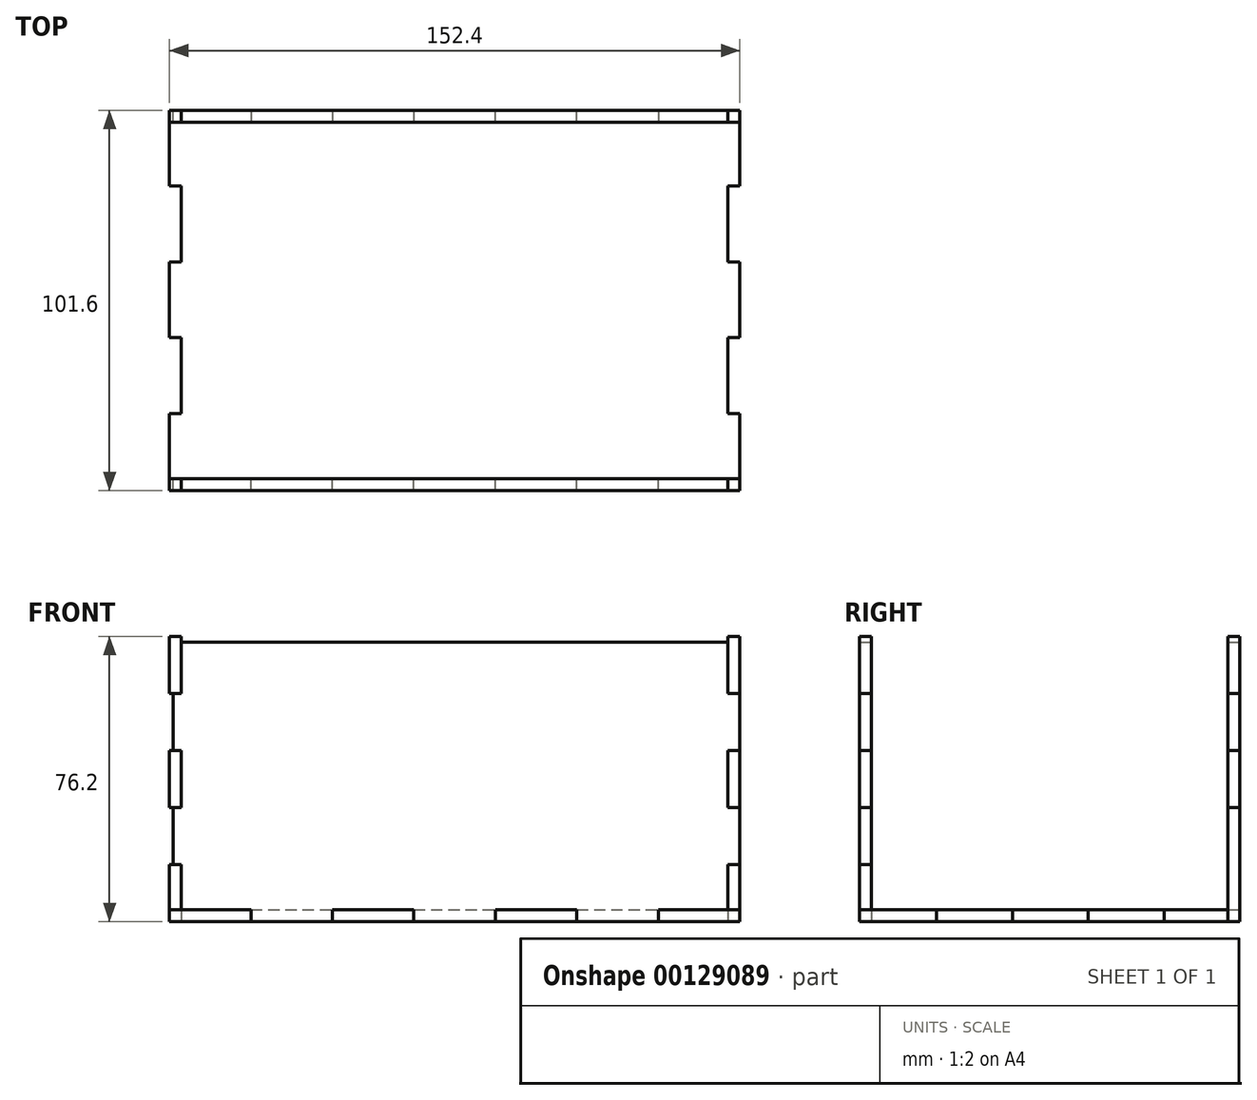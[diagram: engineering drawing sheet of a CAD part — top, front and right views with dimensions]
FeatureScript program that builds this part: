
annotation { "Feature Type Name" : "Feature", "Feature Type Description" : "" }
export const myFeature = defineFeature(function(context is Context, id is Id, definition is map)
    precondition{}
    {
        {
            var Q0;
            Q0=qCreatedBy(makeId("Top.planeOp"),FACE);
            var sketch = newSketch(context, id + "F0", { "sketchPlane" : qUnion([Q0])});
            skLineSegment(sketch, "E0.bottom", {"start": v(76.2, 50.8) * mm, "end": v(-76.2, 50.8) * mm});
            skLineSegment(sketch, "E0.top", {"start": v(76.2, -50.8) * mm, "end": v(-76.2, -50.8) * mm});
            skLineSegment(sketch, "E0.left", {"start": v(76.2, 50.8) * mm, "end": v(76.2, -50.8) * mm});
            skLineSegment(sketch, "E0.right", {"start": v(-76.2, 50.8) * mm, "end": v(-76.2, -50.8) * mm});
            skPoint(sketch, "E0.middle", {"position": v(0, 0) * mm});
            skLineSegment(sketch, "E1", {"start": v(-76.2, 50.8) * mm, "end": v(-73.03, 50.8) * mm});
            skLineSegment(sketch, "E2.0.1.0", {"start": v(-76.2, 30.55) * mm, "end": v(-73.03, 30.55) * mm});
            skLineSegment(sketch, "E2.0.2.0", {"start": v(-76.2, 10.3) * mm, "end": v(-73.03, 10.3) * mm});
            skLineSegment(sketch, "E2.0.3.0", {"start": v(-76.2, -9.95) * mm, "end": v(-73.03, -9.95) * mm});
            skLineSegment(sketch, "E2.0.4.0", {"start": v(-76.2, -30.2) * mm, "end": v(-73.03, -30.2) * mm});
            skLineSegment(sketch, "E2.0.5.0", {"start": v(-76.2, -50.45) * mm, "end": v(-73.03, -50.45) * mm});
            skLineSegment(sketch, "E2.direction1", {"start": v(-76.2, 50.8) * mm, "end": v(-47.87, 50.8) * mm});
            skLineSegment(sketch, "E2.direction2", {"start": v(-76.2, 50.8) * mm, "end": v(-76.2, 30.55) * mm, "construction": true});
            skLineSegment(sketch, "E3", {"start": v(-73.03, 50.8) * mm, "end": v(-73.03, -50.45) * mm});
            skLineSegment(sketch, "E4.MirrorCS", {"start": v(76.2, 50.8) * mm, "end": v(73.03, 50.8) * mm});
            skLineSegment(sketch, "E5.MirrorCS", {"start": v(76.2, -50.45) * mm, "end": v(73.03, -50.45) * mm});
            skLineSegment(sketch, "E6.MirrorCS", {"start": v(76.2, 30.55) * mm, "end": v(73.03, 30.55) * mm});
            skLineSegment(sketch, "E7.MirrorCS", {"start": v(76.2, -9.95) * mm, "end": v(73.03, -9.95) * mm});
            skLineSegment(sketch, "E8.MirrorCS", {"start": v(76.2, 10.3) * mm, "end": v(73.03, 10.3) * mm});
            skLineSegment(sketch, "E9.MirrorCS", {"start": v(76.2, -30.2) * mm, "end": v(73.03, -30.2) * mm});
            skLineSegment(sketch, "E10.MirrorCS", {"start": v(73.03, 50.8) * mm, "end": v(73.03, -50.45) * mm});
            skLineSegment(sketch, "E11.MirrorCS", {"start": v(76.2, 50.8) * mm, "end": v(76.2, 30.55) * mm, "construction": true});
            skLineSegment(sketch, "E12", {"start": v(-76.2, 50.8) * mm, "end": v(-76.2, 47.63) * mm});
            skLineSegment(sketch, "E13.1.0.0", {"start": v(-54.43, 50.8) * mm, "end": v(-54.43, 47.63) * mm});
            skLineSegment(sketch, "E13.2.0.0", {"start": v(-32.66, 50.8) * mm, "end": v(-32.66, 47.63) * mm});
            skLineSegment(sketch, "E13.3.0.0", {"start": v(-10.89, 50.8) * mm, "end": v(-10.89, 47.63) * mm});
            skLineSegment(sketch, "E13.4.0.0", {"start": v(10.89, 50.8) * mm, "end": v(10.89, 47.63) * mm});
            skLineSegment(sketch, "E13.5.0.0", {"start": v(32.66, 50.8) * mm, "end": v(32.66, 47.63) * mm});
            skLineSegment(sketch, "E13.6.0.0", {"start": v(54.43, 50.8) * mm, "end": v(54.43, 47.63) * mm});
            skLineSegment(sketch, "E13.7.0.0", {"start": v(76.2, 50.8) * mm, "end": v(76.2, 47.63) * mm});
            skLineSegment(sketch, "E13.direction1", {"start": v(-76.2, 47.62) * mm, "end": v(-54.43, 47.62) * mm, "construction": true});
            skLineSegment(sketch, "E14", {"start": v(-76.2, 47.62) * mm, "end": v(76.2, 47.63) * mm});
            skLineSegment(sketch, "E15.MirrorCS", {"start": v(76.2, -50.8) * mm, "end": v(76.2, -47.63) * mm});
            skLineSegment(sketch, "E16.MirrorCS", {"start": v(-76.2, -50.8) * mm, "end": v(-73.03, -50.8) * mm});
            skLineSegment(sketch, "E17.MirrorCS", {"start": v(-76.2, -50.8) * mm, "end": v(-76.2, -47.63) * mm});
            skLineSegment(sketch, "E18.MirrorCS", {"start": v(76.2, -50.8) * mm, "end": v(73.03, -50.8) * mm});
            skLineSegment(sketch, "E19.MirrorCS", {"start": v(-54.43, -50.8) * mm, "end": v(-54.43, -47.63) * mm});
            skLineSegment(sketch, "E20.MirrorCS", {"start": v(-32.66, -50.8) * mm, "end": v(-32.66, -47.63) * mm});
            skLineSegment(sketch, "E21.MirrorCS", {"start": v(54.43, -50.8) * mm, "end": v(54.43, -47.63) * mm});
            skLineSegment(sketch, "E22.MirrorCS", {"start": v(32.66, -50.8) * mm, "end": v(32.66, -47.63) * mm});
            skLineSegment(sketch, "E23.MirrorCS", {"start": v(-10.89, -50.8) * mm, "end": v(-10.89, -47.63) * mm});
            skLineSegment(sketch, "E24.MirrorCS", {"start": v(10.89, -50.8) * mm, "end": v(10.89, -47.63) * mm});
            skLineSegment(sketch, "E25.MirrorCS", {"start": v(-76.2, -47.62) * mm, "end": v(-54.43, -47.62) * mm, "construction": true});
            skLineSegment(sketch, "E26.MirrorCS", {"start": v(-76.2, -47.62) * mm, "end": v(76.2, -47.63) * mm});
            skLineSegment(sketch, "E27.MirrorCS", {"start": v(-76.2, -50.8) * mm, "end": v(-47.87, -50.8) * mm});
            skSolve(sketch);
        }
        {
            var Q0;
            {var subQ3=sQuery(id+"F0.wireOp",EDGE,"E2.0.1.0");Q0=makeQuery(id+"F0.imprint","IMPRINT",FACE,{"disambiguationData":[TD([[makeQuery(id+"F0.imprint","IMPRINT",EDGE,{"derivedFrom":subQ3}),1.0]])]});}
            var Q1;
            {var subQ3=sQuery(id+"F0.wireOp",EDGE,"E13.1.0.0");Q1=makeQuery(id+"F0.imprint","IMPRINT",FACE,{"disambiguationData":[TD([[makeQuery(id+"F0.imprint","IMPRINT",EDGE,{"derivedFrom":subQ3}),-1.0]])]});}
            var Q2;
            {var subQ0=sQuery(id+"F0.wireOp",EDGE,"E12");Q2=makeQuery(id+"F0.imprint","IMPRINT",FACE,{"disambiguationData":[TD([[makeQuery(id+"F0.imprint","IMPRINT",EDGE,{"derivedFrom":subQ0}),1.0]])]});}
            var Q3;
            {var subQ0=sQuery(id+"F0.wireOp",EDGE,"E13.2.0.0");Q3=makeQuery(id+"F0.imprint","IMPRINT",FACE,{"disambiguationData":[TD([[makeQuery(id+"F0.imprint","IMPRINT",EDGE,{"derivedFrom":subQ0}),1.0]])]});}
            var Q4;
            {var subQ15=sQuery(id+"F0.wireOp",EDGE,"E3");var subQ24=makeQuery(id+"F0.imprint","INTERSECT",VERTEX,{"derivedFrom":[sQuery(id+"F0.wireOp",EDGE,"E2.0.1.0"),subQ15]});Q4=makeQuery(id+"F0.imprint","IMPRINT",FACE,{"disambiguationData":[TD([[makeQuery(id+"F0.imprint","IMPRINT",EDGE,{"disambiguationData":[TD([[subQ24,1.0]])],"derivedFrom":subQ15}),1.0]])]});}
            var Q5;
            {var subQ0=sQuery(id+"F0.wireOp",EDGE,"E13.4.0.0");Q5=makeQuery(id+"F0.imprint","IMPRINT",FACE,{"disambiguationData":[TD([[makeQuery(id+"F0.imprint","IMPRINT",EDGE,{"derivedFrom":subQ0}),1.0]])]});}
            var Q6;
            {var subQ3=sQuery(id+"F0.wireOp",EDGE,"E13.6.0.0");Q6=makeQuery(id+"F0.imprint","IMPRINT",FACE,{"disambiguationData":[TD([[makeQuery(id+"F0.imprint","IMPRINT",EDGE,{"derivedFrom":subQ3}),1.0]])]});}
            var Q7;
            {var subQ0=sQuery(id+"F0.wireOp",EDGE,"E4.MirrorCS");Q7=makeQuery(id+"F0.imprint","IMPRINT",FACE,{"disambiguationData":[TD([[makeQuery(id+"F0.imprint","IMPRINT",EDGE,{"derivedFrom":subQ0}),1.0]])]});}
            var Q8;
            {var subQ0=sQuery(id+"F0.wireOp",EDGE,"E6.MirrorCS");Q8=makeQuery(id+"F0.imprint","IMPRINT",FACE,{"disambiguationData":[TD([[makeQuery(id+"F0.imprint","IMPRINT",EDGE,{"derivedFrom":subQ0}),-1.0]])]});}
            var Q9;
            {var subQ0=sQuery(id+"F0.wireOp",EDGE,"E7.MirrorCS");Q9=makeQuery(id+"F0.imprint","IMPRINT",FACE,{"disambiguationData":[TD([[makeQuery(id+"F0.imprint","IMPRINT",EDGE,{"derivedFrom":subQ0}),-1.0]])]});}
            var Q10;
            {var subQ0=sQuery(id+"F0.wireOp",EDGE,"E9.MirrorCS");Q10=makeQuery(id+"F0.imprint","IMPRINT",FACE,{"disambiguationData":[TD([[makeQuery(id+"F0.imprint","IMPRINT",EDGE,{"derivedFrom":subQ0}),1.0]])]});}
            var Q11;
            {var subQ0=sQuery(id+"F0.wireOp",EDGE,"E5.MirrorCS");Q11=makeQuery(id+"F0.imprint","IMPRINT",FACE,{"disambiguationData":[TD([[makeQuery(id+"F0.imprint","IMPRINT",EDGE,{"derivedFrom":subQ0}),-1.0]])]});}
            var Q12;
            {var subQ2=sQuery(id+"F0.wireOp",EDGE,"E5.MirrorCS");Q12=makeQuery(id+"F0.imprint","IMPRINT",FACE,{"disambiguationData":[TD([[makeQuery(id+"F0.imprint","IMPRINT",EDGE,{"derivedFrom":subQ2}),1.0]])]});}
            var Q13;
            {var subQ0=sQuery(id+"F0.wireOp",EDGE,"E22.MirrorCS");Q13=makeQuery(id+"F0.imprint","IMPRINT",FACE,{"disambiguationData":[TD([[makeQuery(id+"F0.imprint","IMPRINT",EDGE,{"derivedFrom":subQ0}),1.0]])]});}
            var Q14;
            {var subQ0=sQuery(id+"F0.wireOp",EDGE,"E20.MirrorCS");Q14=makeQuery(id+"F0.imprint","IMPRINT",FACE,{"disambiguationData":[TD([[makeQuery(id+"F0.imprint","IMPRINT",EDGE,{"derivedFrom":subQ0}),-1.0]])]});}
            var Q15;
            {var subQ5=sQuery(id+"F0.wireOp",EDGE,"E2.0.5.0");Q15=makeQuery(id+"F0.imprint","IMPRINT",FACE,{"disambiguationData":[TD([[makeQuery(id+"F0.imprint","IMPRINT",EDGE,{"derivedFrom":subQ5}),-1.0]])]});}
            var Q16;
            {var subQ0=sQuery(id+"F0.wireOp",EDGE,"E2.0.5.0");Q16=makeQuery(id+"F0.imprint","IMPRINT",FACE,{"disambiguationData":[TD([[makeQuery(id+"F0.imprint","IMPRINT",EDGE,{"derivedFrom":subQ0}),1.0]])]});}
            var Q17;
            {var subQ3=sQuery(id+"F0.wireOp",EDGE,"E2.0.4.0");Q17=makeQuery(id+"F0.imprint","IMPRINT",FACE,{"disambiguationData":[TD([[makeQuery(id+"F0.imprint","IMPRINT",EDGE,{"derivedFrom":subQ3}),-1.0]])]});}
            var Q18;
            {var subQ0=sQuery(id+"F0.wireOp",EDGE,"E2.0.2.0");Q18=makeQuery(id+"F0.imprint","IMPRINT",FACE,{"disambiguationData":[TD([[makeQuery(id+"F0.imprint","IMPRINT",EDGE,{"derivedFrom":subQ0}),-1.0]])]});}
            extrude(context, id + "F1", {"entities" : qUnion([Q0, Q1, Q2, Q3, Q4, Q5, Q6, Q7, Q8, Q9, Q10, Q11, Q12, Q13, Q14, Q15, Q16, Q17, Q18]), "depth" : 3.17 * mm});
        }
        {
            var Q0;
            Q0=makeQuery(id+"F1.opExtrude","SWEPT_FACE",FACE,{"disambiguationData":[OSD([sQuery(id+"F0.wireOp",EDGE,"E0.left"),sQuery(id+"F0.wireOp",EDGE,"E15.MirrorCS")])]});
            var sketch = newSketch(context, id + "F2", { "sketchPlane" : qUnion([Q0])});
            skLineSegment(sketch, "E28.bottom", {"start": v(-50.8, 0) * mm, "end": v(50.8, 0) * mm});
            skLineSegment(sketch, "E28.top", {"start": v(-50.8, 76.2) * mm, "end": v(50.8, 76.2) * mm});
            skLineSegment(sketch, "E28.left", {"start": v(-50.8, 0) * mm, "end": v(-50.8, 76.2) * mm});
            skLineSegment(sketch, "E28.right", {"start": v(50.8, 0) * mm, "end": v(50.8, 76.2) * mm});
            skLineSegment(sketch, "E29", {"start": v(-50.8, 76.2) * mm, "end": v(-47.63, 76.2) * mm});
            skLineSegment(sketch, "E30.0.1.0", {"start": v(-50.8, 60.96) * mm, "end": v(-47.63, 60.96) * mm});
            skLineSegment(sketch, "E30.0.2.0", {"start": v(-50.8, 45.72) * mm, "end": v(-47.63, 45.72) * mm});
            skLineSegment(sketch, "E30.0.3.0", {"start": v(-50.8, 30.48) * mm, "end": v(-47.63, 30.48) * mm});
            skLineSegment(sketch, "E30.0.4.0", {"start": v(-50.8, 15.24) * mm, "end": v(-47.63, 15.24) * mm});
            skLineSegment(sketch, "E30.0.5.0", {"start": v(-50.8, 0) * mm, "end": v(-47.63, 0) * mm});
            skLineSegment(sketch, "E30.direction1", {"start": v(-50.8, 76.2) * mm, "end": v(-25.4, 76.2) * mm, "construction": true});
            skLineSegment(sketch, "E30.direction2", {"start": v(-50.8, 76.2) * mm, "end": v(-50.8, 60.96) * mm, "construction": true});
            skLineSegment(sketch, "E31", {"start": v(-47.63, 0) * mm, "end": v(-47.63, 76.2) * mm});
            skLineSegment(sketch, "E32.MirrorCS", {"start": v(50.8, 76.2) * mm, "end": v(47.63, 76.2) * mm});
            skLineSegment(sketch, "E33.MirrorCS", {"start": v(50.8, 0) * mm, "end": v(47.63, 0) * mm});
            skLineSegment(sketch, "E34.MirrorCS", {"start": v(50.8, 60.96) * mm, "end": v(47.63, 60.96) * mm});
            skLineSegment(sketch, "E35.MirrorCS", {"start": v(50.8, 45.72) * mm, "end": v(47.63, 45.72) * mm});
            skLineSegment(sketch, "E36.MirrorCS", {"start": v(50.8, 30.48) * mm, "end": v(47.63, 30.48) * mm});
            skLineSegment(sketch, "E37.MirrorCS", {"start": v(50.8, 15.24) * mm, "end": v(47.63, 15.24) * mm});
            skLineSegment(sketch, "E38.MirrorCS", {"start": v(47.63, 0) * mm, "end": v(47.63, 76.2) * mm});
            skLineSegment(sketch, "E39.MirrorCS", {"start": v(50.8, 76.2) * mm, "end": v(50.8, 60.96) * mm, "construction": true});
            skSolve(sketch);
        }
        {
            var Q0;
            {var subQ4=sQuery(id+"F2.wireOp",EDGE,"E28.top");Q0=makeQuery(id+"F2.imprint","IMPRINT",FACE,{"disambiguationData":[TD([[makeQuery(id+"F2.imprint","IMPRINT",EDGE,{"derivedFrom":subQ4}),-1.0]])]});}
            var Q1;
            {var subQ0=sQuery(id+"F2.wireOp",EDGE,"E29");Q1=makeQuery(id+"F2.imprint","IMPRINT",FACE,{"disambiguationData":[TD([[makeQuery(id+"F2.imprint","IMPRINT",EDGE,{"derivedFrom":subQ0}),-1.0]])]});}
            var Q2;
            {var subQ0=sQuery(id+"F2.wireOp",EDGE,"E30.0.2.0");Q2=makeQuery(id+"F2.imprint","IMPRINT",FACE,{"disambiguationData":[TD([[makeQuery(id+"F2.imprint","IMPRINT",EDGE,{"derivedFrom":subQ0}),-1.0]])]});}
            var Q3;
            {var subQ3=sQuery(id+"F2.wireOp",EDGE,"E30.0.4.0");Q3=makeQuery(id+"F2.imprint","IMPRINT",FACE,{"disambiguationData":[TD([[makeQuery(id+"F2.imprint","IMPRINT",EDGE,{"derivedFrom":subQ3}),-1.0]])]});}
            var Q4;
            {var subQ0=sQuery(id+"F2.wireOp",EDGE,"E32.MirrorCS");Q4=makeQuery(id+"F2.imprint","IMPRINT",FACE,{"disambiguationData":[TD([[makeQuery(id+"F2.imprint","IMPRINT",EDGE,{"derivedFrom":subQ0}),1.0]])]});}
            var Q5;
            {var subQ0=sQuery(id+"F2.wireOp",EDGE,"E35.MirrorCS");Q5=makeQuery(id+"F2.imprint","IMPRINT",FACE,{"disambiguationData":[TD([[makeQuery(id+"F2.imprint","IMPRINT",EDGE,{"derivedFrom":subQ0}),1.0]])]});}
            var Q6;
            {var subQ0=sQuery(id+"F2.wireOp",EDGE,"E33.MirrorCS");Q6=makeQuery(id+"F2.imprint","IMPRINT",FACE,{"disambiguationData":[TD([[makeQuery(id+"F2.imprint","IMPRINT",EDGE,{"derivedFrom":subQ0}),-1.0]])]});}
            extrude(context, id + "F3", {"entities" : qUnion([Q0, Q1, Q2, Q3, Q4, Q5, Q6]), "oppositeDirection" : true, "depth" : 3.17 * mm});
        }
        {
            var Q0;
            Q0=makeQuery(id+"F3.opExtrude","SWEPT_BODY",BODY,{"disambiguationData":[OSD([sQuery(id+"F0.wireOp",EDGE,"E9.MirrorCS"),sQuery(id+"F0.wireOp",EDGE,"E0.left"),sQuery(id+"F0.wireOp",EDGE,"E15.MirrorCS"),sQuery(id+"F2.wireOp",EDGE,"E28.bottom"),sQuery(id+"F2.wireOp",EDGE,"E28.top"),sQuery(id+"F2.wireOp",EDGE,"E28.left"),sQuery(id+"F2.wireOp",EDGE,"E29"),sQuery(id+"F2.wireOp",EDGE,"E30.0.1.0"),sQuery(id+"F2.wireOp",EDGE,"E30.0.2.0"),sQuery(id+"F2.wireOp",EDGE,"E30.0.3.0"),sQuery(id+"F2.wireOp",EDGE,"E30.0.4.0"),sQuery(id+"F2.wireOp",EDGE,"E31"),sQuery(id+"F2.wireOp",EDGE,"E32.MirrorCS"),sQuery(id+"F2.wireOp",EDGE,"E33.MirrorCS"),sQuery(id+"F2.wireOp",EDGE,"E34.MirrorCS"),sQuery(id+"F2.wireOp",EDGE,"E35.MirrorCS"),sQuery(id+"F2.wireOp",EDGE,"E36.MirrorCS"),sQuery(id+"F2.wireOp",EDGE,"E37.MirrorCS"),sQuery(id+"F2.wireOp",EDGE,"E28.right"),sQuery(id+"F2.wireOp",EDGE,"E38.MirrorCS")])]});
            var Q1;
            Q1=qCreatedBy(makeId("Right.planeOp"),FACE);
            mirror(context, id + "F4", {"entities" : qUnion([Q0]), "mirrorPlane" : qUnion([Q1])});
        }
        {
            var Q0;
            Q0=makeQuery(id+"F1.opExtrude","SWEPT_BODY",BODY,{"disambiguationData":[OSD([sQuery(id+"F0.wireOp",EDGE,"E0.bottom"),sQuery(id+"F0.wireOp",EDGE,"E0.right"),sQuery(id+"F0.wireOp",EDGE,"E2.0.1.0"),sQuery(id+"F0.wireOp",EDGE,"E2.0.2.0"),sQuery(id+"F0.wireOp",EDGE,"E2.0.3.0"),sQuery(id+"F0.wireOp",EDGE,"E2.0.4.0"),sQuery(id+"F0.wireOp",EDGE,"E2.direction1"),sQuery(id+"F0.wireOp",EDGE,"E3"),sQuery(id+"F0.wireOp",EDGE,"E4.MirrorCS"),sQuery(id+"F0.wireOp",EDGE,"E6.MirrorCS"),sQuery(id+"F0.wireOp",EDGE,"E7.MirrorCS"),sQuery(id+"F0.wireOp",EDGE,"E8.MirrorCS"),sQuery(id+"F0.wireOp",EDGE,"E9.MirrorCS"),sQuery(id+"F0.wireOp",EDGE,"E10.MirrorCS"),sQuery(id+"F0.wireOp",EDGE,"E0.left"),sQuery(id+"F0.wireOp",EDGE,"E12"),sQuery(id+"F0.wireOp",EDGE,"E13.1.0.0"),sQuery(id+"F0.wireOp",EDGE,"E13.2.0.0"),sQuery(id+"F0.wireOp",EDGE,"E13.3.0.0"),sQuery(id+"F0.wireOp",EDGE,"E13.4.0.0"),sQuery(id+"F0.wireOp",EDGE,"E13.5.0.0"),sQuery(id+"F0.wireOp",EDGE,"E13.6.0.0"),sQuery(id+"F0.wireOp",EDGE,"E13.7.0.0"),sQuery(id+"F0.wireOp",EDGE,"E14"),sQuery(id+"F0.wireOp",EDGE,"E15.MirrorCS"),sQuery(id+"F0.wireOp",EDGE,"E17.MirrorCS"),sQuery(id+"F0.wireOp",EDGE,"E19.MirrorCS"),sQuery(id+"F0.wireOp",EDGE,"E20.MirrorCS"),sQuery(id+"F0.wireOp",EDGE,"E21.MirrorCS"),sQuery(id+"F0.wireOp",EDGE,"E22.MirrorCS"),sQuery(id+"F0.wireOp",EDGE,"E23.MirrorCS"),sQuery(id+"F0.wireOp",EDGE,"E24.MirrorCS"),sQuery(id+"F0.wireOp",EDGE,"E26.MirrorCS"),sQuery(id+"F0.wireOp",EDGE,"E0.top")])]});
            var Q1;
            Q1=makeQuery(id+"F3.opExtrude","SWEPT_BODY",BODY,{"disambiguationData":[OSD([sQuery(id+"F0.wireOp",EDGE,"E9.MirrorCS"),sQuery(id+"F0.wireOp",EDGE,"E0.left"),sQuery(id+"F0.wireOp",EDGE,"E15.MirrorCS"),sQuery(id+"F2.wireOp",EDGE,"E28.bottom"),sQuery(id+"F2.wireOp",EDGE,"E28.top"),sQuery(id+"F2.wireOp",EDGE,"E28.left"),sQuery(id+"F2.wireOp",EDGE,"E29"),sQuery(id+"F2.wireOp",EDGE,"E30.0.1.0"),sQuery(id+"F2.wireOp",EDGE,"E30.0.2.0"),sQuery(id+"F2.wireOp",EDGE,"E30.0.3.0"),sQuery(id+"F2.wireOp",EDGE,"E30.0.4.0"),sQuery(id+"F2.wireOp",EDGE,"E31"),sQuery(id+"F2.wireOp",EDGE,"E32.MirrorCS"),sQuery(id+"F2.wireOp",EDGE,"E33.MirrorCS"),sQuery(id+"F2.wireOp",EDGE,"E34.MirrorCS"),sQuery(id+"F2.wireOp",EDGE,"E35.MirrorCS"),sQuery(id+"F2.wireOp",EDGE,"E36.MirrorCS"),sQuery(id+"F2.wireOp",EDGE,"E37.MirrorCS"),sQuery(id+"F2.wireOp",EDGE,"E28.right"),sQuery(id+"F2.wireOp",EDGE,"E38.MirrorCS")])]});
            var Q2;
            Q2=makeQuery(id+"F4.opPattern","COPY",BODY,{"derivedFrom":makeQuery(id+"F3.opExtrude","SWEPT_BODY",BODY,{"disambiguationData":[OSD([sQuery(id+"F0.wireOp",EDGE,"E9.MirrorCS"),sQuery(id+"F0.wireOp",EDGE,"E0.left"),sQuery(id+"F0.wireOp",EDGE,"E15.MirrorCS"),sQuery(id+"F2.wireOp",EDGE,"E28.bottom"),sQuery(id+"F2.wireOp",EDGE,"E28.top"),sQuery(id+"F2.wireOp",EDGE,"E28.left"),sQuery(id+"F2.wireOp",EDGE,"E29"),sQuery(id+"F2.wireOp",EDGE,"E30.0.1.0"),sQuery(id+"F2.wireOp",EDGE,"E30.0.2.0"),sQuery(id+"F2.wireOp",EDGE,"E30.0.3.0"),sQuery(id+"F2.wireOp",EDGE,"E30.0.4.0"),sQuery(id+"F2.wireOp",EDGE,"E31"),sQuery(id+"F2.wireOp",EDGE,"E32.MirrorCS"),sQuery(id+"F2.wireOp",EDGE,"E33.MirrorCS"),sQuery(id+"F2.wireOp",EDGE,"E34.MirrorCS"),sQuery(id+"F2.wireOp",EDGE,"E35.MirrorCS"),sQuery(id+"F2.wireOp",EDGE,"E36.MirrorCS"),sQuery(id+"F2.wireOp",EDGE,"E37.MirrorCS"),sQuery(id+"F2.wireOp",EDGE,"E28.right"),sQuery(id+"F2.wireOp",EDGE,"E38.MirrorCS")])]}),"instanceName":"1"});
            booleanBodies(context, id + "F5", {"operationType" : BooleanOperationType.SUBTRACTION, "tools" : qUnion([Q0]), "targets" : qUnion([Q1, Q2]), "keepTools" : true});
        }
        {
            var Q0;
            Q0=makeQuery(id+"F1.opExtrude","SWEPT_FACE",FACE,{"disambiguationData":[OSD([sQuery(id+"F0.wireOp",EDGE,"E0.bottom"),sQuery(id+"F0.wireOp",EDGE,"E4.MirrorCS")])]});
            var sketch = newSketch(context, id + "F6", { "sketchPlane" : qUnion([Q0])});
            skLineSegment(sketch, "E40.bottom", {"start": v(-76.2, 74.64) * mm, "end": v(75.17, 74.64) * mm});
            skLineSegment(sketch, "E40.top", {"start": v(-76.2, 0) * mm, "end": v(75.17, 0) * mm});
            skLineSegment(sketch, "E40.left", {"start": v(-76.2, 74.64) * mm, "end": v(-76.2, 0) * mm});
            skLineSegment(sketch, "E40.right", {"start": v(75.17, 74.64) * mm, "end": v(75.17, 0) * mm});
            skSolve(sketch);
        }
        {
            var Q0;
            {var subQ4=sQuery(id+"F6.wireOp",EDGE,"E40.bottom");Q0=makeQuery(id+"F6.imprint","IMPRINT",FACE,{"disambiguationData":[TD([[makeQuery(id+"F6.imprint","IMPRINT",EDGE,{"derivedFrom":subQ4}),-1.0]])]});}
            extrude(context, id + "F7", {"entities" : qUnion([Q0]), "oppositeDirection" : true, "depth" : 3.17 * mm});
        }
        {
            var Q0;
            Q0=makeQuery(id+"F7.opExtrude","SWEPT_BODY",BODY,{"disambiguationData":[OSD([sQuery(id+"F0.wireOp",EDGE,"E0.bottom"),sQuery(id+"F0.wireOp",EDGE,"E4.MirrorCS"),sQuery(id+"F0.wireOp",EDGE,"E13.6.0.0"),sQuery(id+"F6.wireOp",EDGE,"E40.bottom"),sQuery(id+"F6.wireOp",EDGE,"E40.top"),sQuery(id+"F6.wireOp",EDGE,"E40.left"),sQuery(id+"F6.wireOp",EDGE,"E40.right")])]});
            var Q1;
            Q1=qCreatedBy(makeId("Front.planeOp"),FACE);
            mirror(context, id + "F8", {"entities" : qUnion([Q0]), "mirrorPlane" : qUnion([Q1])});
        }
        {
            var Q0;
            Q0=makeQuery(id+"F3.opExtrude","SWEPT_BODY",BODY,{"disambiguationData":[OSD([sQuery(id+"F0.wireOp",EDGE,"E9.MirrorCS"),sQuery(id+"F0.wireOp",EDGE,"E0.left"),sQuery(id+"F0.wireOp",EDGE,"E15.MirrorCS"),sQuery(id+"F2.wireOp",EDGE,"E28.bottom"),sQuery(id+"F2.wireOp",EDGE,"E28.top"),sQuery(id+"F2.wireOp",EDGE,"E28.left"),sQuery(id+"F2.wireOp",EDGE,"E29"),sQuery(id+"F2.wireOp",EDGE,"E30.0.1.0"),sQuery(id+"F2.wireOp",EDGE,"E30.0.2.0"),sQuery(id+"F2.wireOp",EDGE,"E30.0.3.0"),sQuery(id+"F2.wireOp",EDGE,"E30.0.4.0"),sQuery(id+"F2.wireOp",EDGE,"E31"),sQuery(id+"F2.wireOp",EDGE,"E32.MirrorCS"),sQuery(id+"F2.wireOp",EDGE,"E33.MirrorCS"),sQuery(id+"F2.wireOp",EDGE,"E34.MirrorCS"),sQuery(id+"F2.wireOp",EDGE,"E35.MirrorCS"),sQuery(id+"F2.wireOp",EDGE,"E36.MirrorCS"),sQuery(id+"F2.wireOp",EDGE,"E37.MirrorCS"),sQuery(id+"F2.wireOp",EDGE,"E28.right"),sQuery(id+"F2.wireOp",EDGE,"E38.MirrorCS")])]});
            var Q1;
            Q1=makeQuery(id+"F1.opExtrude","SWEPT_BODY",BODY,{"disambiguationData":[OSD([sQuery(id+"F0.wireOp",EDGE,"E0.bottom"),sQuery(id+"F0.wireOp",EDGE,"E0.right"),sQuery(id+"F0.wireOp",EDGE,"E2.0.1.0"),sQuery(id+"F0.wireOp",EDGE,"E2.0.2.0"),sQuery(id+"F0.wireOp",EDGE,"E2.0.3.0"),sQuery(id+"F0.wireOp",EDGE,"E2.0.4.0"),sQuery(id+"F0.wireOp",EDGE,"E2.direction1"),sQuery(id+"F0.wireOp",EDGE,"E3"),sQuery(id+"F0.wireOp",EDGE,"E4.MirrorCS"),sQuery(id+"F0.wireOp",EDGE,"E6.MirrorCS"),sQuery(id+"F0.wireOp",EDGE,"E7.MirrorCS"),sQuery(id+"F0.wireOp",EDGE,"E8.MirrorCS"),sQuery(id+"F0.wireOp",EDGE,"E9.MirrorCS"),sQuery(id+"F0.wireOp",EDGE,"E10.MirrorCS"),sQuery(id+"F0.wireOp",EDGE,"E0.left"),sQuery(id+"F0.wireOp",EDGE,"E12"),sQuery(id+"F0.wireOp",EDGE,"E13.1.0.0"),sQuery(id+"F0.wireOp",EDGE,"E13.2.0.0"),sQuery(id+"F0.wireOp",EDGE,"E13.3.0.0"),sQuery(id+"F0.wireOp",EDGE,"E13.4.0.0"),sQuery(id+"F0.wireOp",EDGE,"E13.5.0.0"),sQuery(id+"F0.wireOp",EDGE,"E13.6.0.0"),sQuery(id+"F0.wireOp",EDGE,"E13.7.0.0"),sQuery(id+"F0.wireOp",EDGE,"E14"),sQuery(id+"F0.wireOp",EDGE,"E15.MirrorCS"),sQuery(id+"F0.wireOp",EDGE,"E17.MirrorCS"),sQuery(id+"F0.wireOp",EDGE,"E19.MirrorCS"),sQuery(id+"F0.wireOp",EDGE,"E20.MirrorCS"),sQuery(id+"F0.wireOp",EDGE,"E21.MirrorCS"),sQuery(id+"F0.wireOp",EDGE,"E22.MirrorCS"),sQuery(id+"F0.wireOp",EDGE,"E23.MirrorCS"),sQuery(id+"F0.wireOp",EDGE,"E24.MirrorCS"),sQuery(id+"F0.wireOp",EDGE,"E26.MirrorCS"),sQuery(id+"F0.wireOp",EDGE,"E0.top")])]});
            var Q2;
            Q2=makeQuery(id+"F4.opPattern","COPY",BODY,{"derivedFrom":makeQuery(id+"F3.opExtrude","SWEPT_BODY",BODY,{"disambiguationData":[OSD([sQuery(id+"F0.wireOp",EDGE,"E9.MirrorCS"),sQuery(id+"F0.wireOp",EDGE,"E0.left"),sQuery(id+"F0.wireOp",EDGE,"E15.MirrorCS"),sQuery(id+"F2.wireOp",EDGE,"E28.bottom"),sQuery(id+"F2.wireOp",EDGE,"E28.top"),sQuery(id+"F2.wireOp",EDGE,"E28.left"),sQuery(id+"F2.wireOp",EDGE,"E29"),sQuery(id+"F2.wireOp",EDGE,"E30.0.1.0"),sQuery(id+"F2.wireOp",EDGE,"E30.0.2.0"),sQuery(id+"F2.wireOp",EDGE,"E30.0.3.0"),sQuery(id+"F2.wireOp",EDGE,"E30.0.4.0"),sQuery(id+"F2.wireOp",EDGE,"E31"),sQuery(id+"F2.wireOp",EDGE,"E32.MirrorCS"),sQuery(id+"F2.wireOp",EDGE,"E33.MirrorCS"),sQuery(id+"F2.wireOp",EDGE,"E34.MirrorCS"),sQuery(id+"F2.wireOp",EDGE,"E35.MirrorCS"),sQuery(id+"F2.wireOp",EDGE,"E36.MirrorCS"),sQuery(id+"F2.wireOp",EDGE,"E37.MirrorCS"),sQuery(id+"F2.wireOp",EDGE,"E28.right"),sQuery(id+"F2.wireOp",EDGE,"E38.MirrorCS")])]}),"instanceName":"1"});
            var Q3;
            Q3=makeQuery(id+"F8.opPattern","COPY",BODY,{"derivedFrom":makeQuery(id+"F7.opExtrude","SWEPT_BODY",BODY,{"disambiguationData":[OSD([sQuery(id+"F0.wireOp",EDGE,"E0.bottom"),sQuery(id+"F0.wireOp",EDGE,"E4.MirrorCS"),sQuery(id+"F0.wireOp",EDGE,"E13.6.0.0"),sQuery(id+"F6.wireOp",EDGE,"E40.bottom"),sQuery(id+"F6.wireOp",EDGE,"E40.top"),sQuery(id+"F6.wireOp",EDGE,"E40.left"),sQuery(id+"F6.wireOp",EDGE,"E40.right")])]}),"instanceName":"1"});
            var Q4;
            Q4=makeQuery(id+"F7.opExtrude","SWEPT_BODY",BODY,{"disambiguationData":[OSD([sQuery(id+"F0.wireOp",EDGE,"E0.bottom"),sQuery(id+"F0.wireOp",EDGE,"E4.MirrorCS"),sQuery(id+"F0.wireOp",EDGE,"E13.6.0.0"),sQuery(id+"F6.wireOp",EDGE,"E40.bottom"),sQuery(id+"F6.wireOp",EDGE,"E40.top"),sQuery(id+"F6.wireOp",EDGE,"E40.left"),sQuery(id+"F6.wireOp",EDGE,"E40.right")])]});
            booleanBodies(context, id + "F9", {"operationType" : BooleanOperationType.SUBTRACTION, "tools" : qUnion([Q0, Q1, Q2]), "targets" : qUnion([Q3, Q4]), "keepTools" : true});
        }
    });
